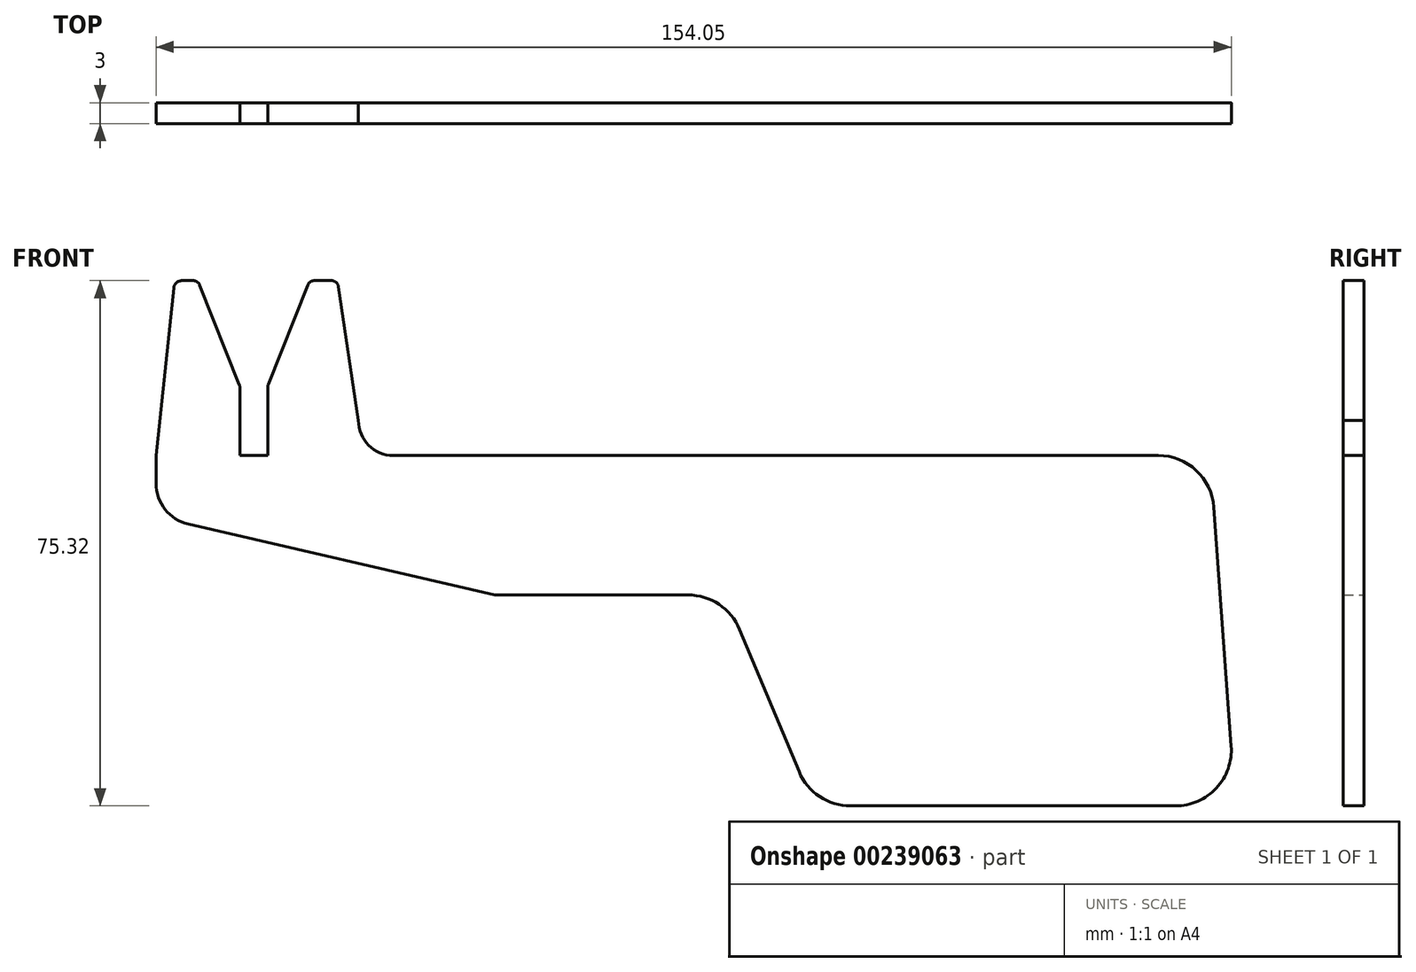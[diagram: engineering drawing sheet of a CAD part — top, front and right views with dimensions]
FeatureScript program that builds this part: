
annotation { "Feature Type Name" : "Feature", "Feature Type Description" : "" }
export const myFeature = defineFeature(function(context is Context, id is Id, definition is map)
    precondition{}
    {
        {
            var Q0;
            Q0=qCreatedBy(makeId("Front.planeOp"),FACE);
            var sketch = newSketch(context, id + "F0", { "sketchPlane" : qUnion([Q0])});
            skLineSegment(sketch, "E0.bottom", {"start": v(-34.44, 6.36) * mm, "end": v(75.13, 6.36) * mm});
            skLineSegment(sketch, "E0.top", {"start": v(-19.62, -13.64) * mm, "end": v(7.78, -13.64) * mm});
            skLineSegment(sketch, "E0.left", {"start": v(-68.44, 6.36) * mm, "end": v(-68.44, 2.36) * mm});
            skPoint(sketch, "E1.visualSharp", {"position": v(-68.44, -13.64) * mm});
            skLineSegment(sketch, "E2.top", {"start": v(-64.7, 31.44) * mm, "end": v(-63.15, 31.44) * mm});
            skPoint(sketch, "E3.visualSharp", {"position": v(-38.44, 6.36) * mm});
            skArc(sketch, "E3.filletArc", {"start": v(-39.44, 11.36) * mm, "mid": v(-37.97, 7.83) * mm, "end": v(-34.44, 6.36) * mm});
            skLineSegment(sketch, "E4", {"start": v(-56.44, 16.16) * mm, "end": v(-56.44, 6.36) * mm});
            skLineSegment(sketch, "E5", {"start": v(-52.44, 16.16) * mm, "end": v(-52.44, 6.36) * mm});
            skLineSegment(sketch, "E6.trimOffspring", {"start": v(-45.73, 31.44) * mm, "end": v(-43.34, 31.44) * mm});
            skLineSegment(sketch, "E7", {"start": v(-56.44, 6.36) * mm, "end": v(-52.44, 6.36) * mm});
            skLineSegment(sketch, "E8", {"start": v(-56.51, 16.55) * mm, "end": v(-62.17, 30.78) * mm});
            skLineSegment(sketch, "E9", {"start": v(-52.36, 16.55) * mm, "end": v(-46.7, 30.78) * mm});
            skLineSegment(sketch, "E10", {"start": v(-42.3, 30.55) * mm, "end": v(-39.44, 11.36) * mm});
            skPoint(sketch, "E2.right.end.orphan", {"position": v(-38.44, 31.44) * mm});
            skPoint(sketch, "E11.visualSharp", {"position": v(-42.44, 31.44) * mm});
            skArc(sketch, "E11.filletArc", {"start": v(-42.3, 30.55) * mm, "mid": v(-42.66, 31.19) * mm, "end": v(-43.34, 31.44) * mm});
            skPoint(sketch, "E12.visualSharp", {"position": v(-46.44, 31.44) * mm});
            skArc(sketch, "E12.filletArc", {"start": v(-45.73, 31.44) * mm, "mid": v(-46.31, 31.26) * mm, "end": v(-46.7, 30.78) * mm});
            skPoint(sketch, "E13.visualSharp", {"position": v(-62.44, 31.44) * mm});
            skArc(sketch, "E13.filletArc", {"start": v(-62.17, 30.78) * mm, "mid": v(-62.56, 31.26) * mm, "end": v(-63.15, 31.44) * mm});
            skPoint(sketch, "E14.visualSharp", {"position": v(-56.44, 16.36) * mm});
            skArc(sketch, "E14.filletArc", {"start": v(-56.44, 16.16) * mm, "mid": v(-56.46, 16.36) * mm, "end": v(-56.51, 16.55) * mm});
            skPoint(sketch, "E15.visualSharp", {"position": v(-52.44, 16.36) * mm});
            skArc(sketch, "E15.filletArc", {"start": v(-52.36, 16.55) * mm, "mid": v(-52.42, 16.36) * mm, "end": v(-52.44, 16.16) * mm});
            skPoint(sketch, "E16.visualSharp", {"position": v(-25.76, -13.64) * mm});
            skPoint(sketch, "E17.visualSharp", {"position": v(-68.44, -3.64) * mm});
            skArc(sketch, "E17.filletArc", {"start": v(-68.44, 2.36) * mm, "mid": v(-67.13, -1.37) * mm, "end": v(-63.79, -3.48) * mm});
            skLineSegment(sketch, "E18", {"start": v(-65.9, 30.35) * mm, "end": v(-68.44, 6.36) * mm});
            skPoint(sketch, "E19.orphan", {"position": v(-68.44, 31.44) * mm});
            skPoint(sketch, "E20.visualSharp", {"position": v(-65.8, 31.44) * mm});
            skArc(sketch, "E20.filletArc", {"start": v(-64.7, 31.44) * mm, "mid": v(-65.51, 31.13) * mm, "end": v(-65.9, 30.35) * mm});
            skLineSegment(sketch, "E21", {"start": v(-19.9, -13.6) * mm, "end": v(-63.79, -3.48) * mm});
            skPoint(sketch, "E22.visualSharp", {"position": v(-19.76, -13.64) * mm});
            skArc(sketch, "E22.filletArc", {"start": v(-19.9, -13.6) * mm, "mid": v(-19.76, -13.63) * mm, "end": v(-19.62, -13.64) * mm});
            skLineSegment(sketch, "E23", {"start": v(15.17, -18.55) * mm, "end": v(23.69, -38.96) * mm});
            skLineSegment(sketch, "E24", {"start": v(31.07, -43.88) * mm, "end": v(77.61, -43.88) * mm});
            skLineSegment(sketch, "E25", {"start": v(85.6, -35.3) * mm, "end": v(83.1, -1.06) * mm});
            skPoint(sketch, "E26.visualSharp", {"position": v(13.11, -13.64) * mm});
            skArc(sketch, "E26.filletArc", {"start": v(15.17, -18.55) * mm, "mid": v(12.22, -14.98) * mm, "end": v(7.78, -13.64) * mm});
            skPoint(sketch, "E27.visualSharp", {"position": v(25.74, -43.88) * mm});
            skArc(sketch, "E27.filletArc", {"start": v(23.69, -38.96) * mm, "mid": v(26.64, -42.54) * mm, "end": v(31.07, -43.88) * mm});
            skPoint(sketch, "E28.visualSharp", {"position": v(86.21, -43.88) * mm});
            skArc(sketch, "E28.filletArc", {"start": v(77.61, -43.88) * mm, "mid": v(83.47, -41.33) * mm, "end": v(85.6, -35.3) * mm});
            skPoint(sketch, "E29.visualSharp", {"position": v(82.57, 6.36) * mm});
            skArc(sketch, "E29.filletArc", {"start": v(83.1, -1.06) * mm, "mid": v(80.58, 4.22) * mm, "end": v(75.13, 6.36) * mm});
            skSolve(sketch);
        }
        {
            var Q0;
            Q0=qSketchRegion(id+"F0",true);
            extrude(context, id + "F1", {"entities" : qUnion([Q0]), "depth" : 3 * mm, "offsetDistance" : 25 * mm});
        }
    });
